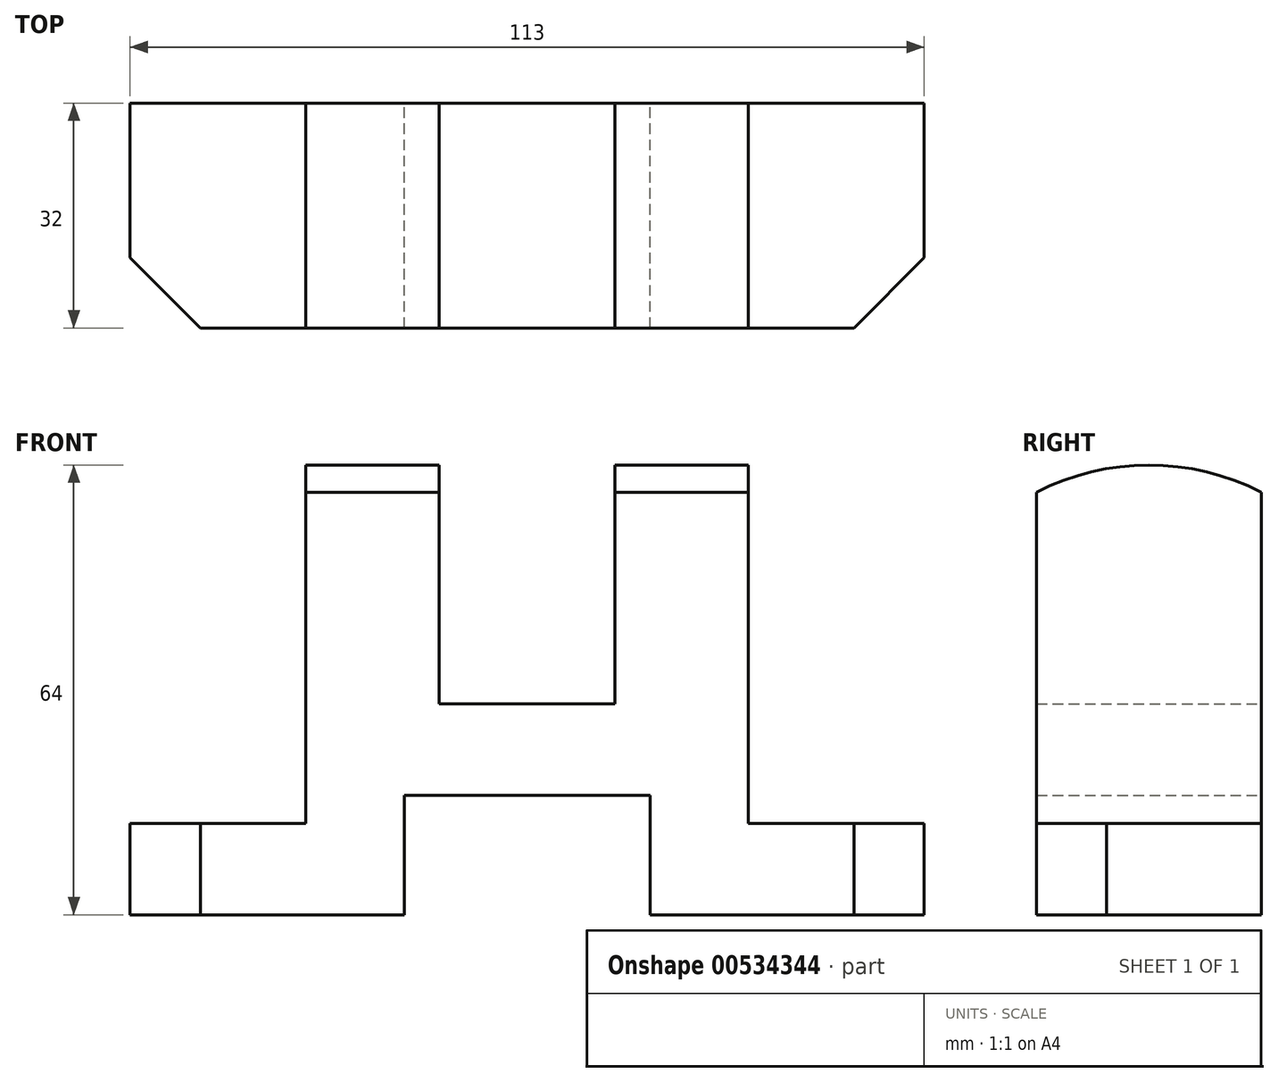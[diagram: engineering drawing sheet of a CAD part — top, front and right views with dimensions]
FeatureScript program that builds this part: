
annotation { "Feature Type Name" : "Feature", "Feature Type Description" : "" }
export const myFeature = defineFeature(function(context is Context, id is Id, definition is map)
    precondition{}
    {
        {
            var Q0;
            Q0=qCreatedBy(makeId("Front.planeOp"),FACE);
            var sketch = newSketch(context, id + "F0", { "sketchPlane" : qUnion([Q0])});
            skLineSegment(sketch, "E0.bottom", {"start": v(-31.5, 32) * mm, "end": v(-12.5, 32) * mm});
            skLineSegment(sketch, "E0.top", {"start": v(-56.5, -32) * mm, "end": v(-17.5, -32) * mm});
            skLineSegment(sketch, "E0.left", {"start": v(-56.5, -19) * mm, "end": v(-56.5, -32) * mm});
            skLineSegment(sketch, "E0.right", {"start": v(56.5, -19) * mm, "end": v(56.5, -32) * mm});
            skPoint(sketch, "E0.middle", {"position": v(0, 0) * mm});
            skLineSegment(sketch, "E1", {"start": v(-56.5, -19) * mm, "end": v(-31.5, -19) * mm});
            skLineSegment(sketch, "E2", {"start": v(-31.5, -19) * mm, "end": v(-31.5, 32) * mm});
            skLineSegment(sketch, "E3", {"start": v(-12.5, 32) * mm, "end": v(-12.5, -2) * mm});
            skLineSegment(sketch, "E4", {"start": v(-12.5, -2) * mm, "end": v(12.5, -2) * mm});
            skLineSegment(sketch, "E5", {"start": v(12.5, -2) * mm, "end": v(12.5, 32) * mm});
            skLineSegment(sketch, "E6", {"start": v(12.5, 32) * mm, "end": v(31.5, 32) * mm});
            skLineSegment(sketch, "E7", {"start": v(31.5, 32) * mm, "end": v(31.5, -19) * mm});
            skLineSegment(sketch, "E8", {"start": v(31.5, -19) * mm, "end": v(56.5, -19) * mm});
            skLineSegment(sketch, "E9", {"start": v(-17.5, -32) * mm, "end": v(-17.5, -15) * mm});
            skLineSegment(sketch, "E10", {"start": v(-17.5, -15) * mm, "end": v(17.5, -15) * mm});
            skLineSegment(sketch, "E11", {"start": v(17.5, -15) * mm, "end": v(17.5, -32) * mm});
            skPoint(sketch, "E12.orphan", {"position": v(-56.5, 32) * mm});
            skPoint(sketch, "E13.orphan", {"position": v(56.5, 32) * mm});
            skLineSegment(sketch, "E14.trimOffspring", {"start": v(17.5, -32) * mm, "end": v(56.5, -32) * mm});
            skSolve(sketch);
        }
        {
            var Q0;
            Q0 = qSketchRegion(id + "F0", true);
            extrude(context, id + "F1", {"entities" : qUnion([Q0]), "depth" : 32 * mm, "offsetDistance" : 25 * mm});
        }
        {
            var Q0;
            Q0=makeQuery(id+"F1.opExtrude","SWEPT_FACE",FACE,{"disambiguationData":[OSD([sQuery(id+"F0.wireOp",EDGE,"E7")])]});
            var sketch = newSketch(context, id + "F2", { "sketchPlane" : qUnion([Q0])});
            skCircle(sketch, "E15", {"center": v(-16, -3) * mm, "radius": 35 * mm});
            skPoint(sketch, "E15.first.point", {"position": v(-16, 32) * mm});
            skPoint(sketch, "E15.second.point", {"position": v(-16, -38) * mm});
            skPoint(sketch, "E15.second.point.positionSnap0", {"position": v(-16, 32) * mm});
            skPoint(sketch, "E15.third.point", {"position": v(-36.93, -31.05) * mm});
            skCircle(sketch, "E16", {"center": v(-16, -3) * mm, "radius": 43.74 * mm});
            skSolve(sketch);
        }
        {
            var Q0;
            Q0 = qSketchRegion(id + "F2", true);
            extrude(context, id + "F3", {"entities" : qUnion([Q0]), "operationType" : NewBodyOperationType.REMOVE, "endBound" : BoundingType.THROUGH_ALL, "oppositeDirection" : true, "depth" : 25 * mm, "offsetDistance" : 25 * mm});
        }
        {
            var Q0;
            Q0=makeQuery(id+"F1.opExtrude","CAP_EDGE",EDGE,{"disambiguationData":[OSD([sQuery(id+"F0.wireOp",EDGE,"E0.left")])],"isStart":false});
            var Q1;
            Q1=makeQuery(id+"F1.opExtrude","CAP_EDGE",EDGE,{"disambiguationData":[OSD([sQuery(id+"F0.wireOp",EDGE,"E0.right")])],"isStart":false});
            chamfer(context, id + "F4", {"entities" : qUnion([Q0, Q1]), "chamferType" : ChamferType.OFFSET_ANGLE, "width" : 10 * mm, "oppositeDirection" : false, "angle" : 45 * degree, "tangentPropagation" : true});
        }
    });
